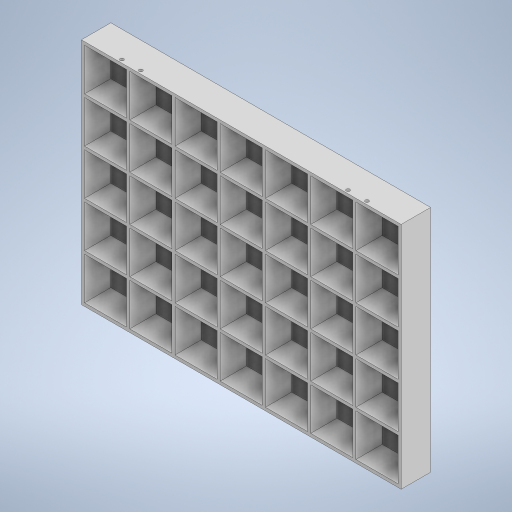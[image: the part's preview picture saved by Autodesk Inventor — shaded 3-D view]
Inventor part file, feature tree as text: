
AUTODESK INVENTOR PART (.ipt)
format: ipt  version: 2024 (Build 280153000, 153)  size: 482,816 bytes
history: native  units: in
note: dims shown in document units (in); Inventor stores cm internally (conversion verified against a paired STEP export)
features: extrude x3, sketch x3
ambient origin geometry x8: Origin, YZ Plane, XZ Plane, XY Plane, X Axis, Y Axis, Z Axis, Center Point
bodies: Solid1 (feature_tree)
feature tree (6):
  extrude  "Extrusion1"  Depth=8.5827in
  extrude  "Extrusion2"  TaperAngle=0.0deg  [1 undecoded]
  extrude  "Extrusion3"  Depth=0.1181in
  sketch  "Sketch1"  dims[d0=11.9685in d1=8.5827in]
  sketch  "Sketch2"  dims[d2=1.1024in d3=0.0in]
  sketch  "Sketch3"  dims[d4=1.5748in d5=0.1181in d6=0.1181in d7=1.5748in d8=2.7559in d10=1.6929in d11=1.9685in d13=1.6929in d16=0.9843in d17=0.0in d20=0.1181in d21=0.1299in d22=0.3543in d23=0.1299in d24=0.3543in d25=0.1299in d31=0.1299in d33=0.3937in d34=0.0in d35=0.7087in d36=1.3976in]
note: 1 required parameter value undecoded (feature->parameter linkage not recoverable at this tier; creation-order binding heuristic only, values carry confidence <= 0.55)
